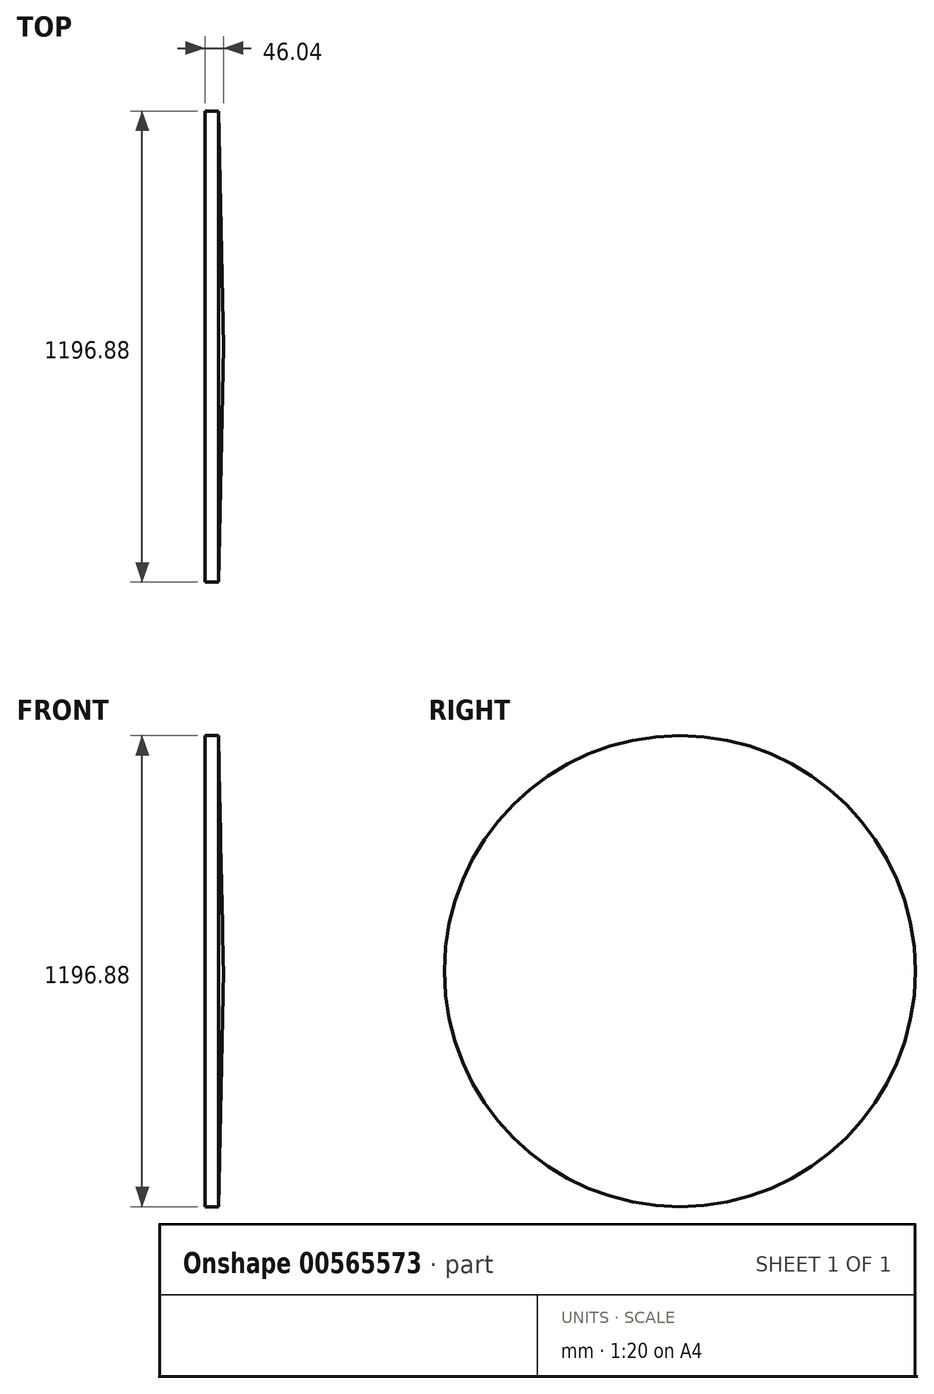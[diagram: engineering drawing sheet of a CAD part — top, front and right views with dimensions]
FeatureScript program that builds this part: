
annotation { "Feature Type Name" : "Feature", "Feature Type Description" : "" }
export const myFeature = defineFeature(function(context is Context, id is Id, definition is map)
    precondition{}
    {
        {
            var Q0;
            Q0=qCreatedBy(makeId("Front.planeOp"),FACE);
            var sketch = newSketch(context, id + "F0", { "sketchPlane" : qUnion([Q0])});
            skPoint(sketch, "E0.middle", {"position": v(0, 0) * mm});
            skLineSegment(sketch, "E1.bottom", {"start": v(-222.31, -598.44) * mm, "end": v(-216.08, -598.44) * mm});
            skLineSegment(sketch, "E1.top", {"start": v(-234.95, 598.44) * mm, "end": v(-230.46, 598.44) * mm});
            skLineSegment(sketch, "E2.bottom", {"start": v(234.95, -632.46) * mm, "end": v(190.65, -632.46) * mm});
            skLineSegment(sketch, "E2.top", {"start": v(222.31, 598.44) * mm, "end": v(188.9, 598.44) * mm});
            skLineSegment(sketch, "E3", {"start": v(0, 0) * mm, "end": v(0, 69.03) * mm});
            skLineSegment(sketch, "E4", {"start": v(-234.95, 0) * mm, "end": v(234.95, 0) * mm});
            skLineSegment(sketch, "E5", {"start": v(-234.95, 598.44) * mm, "end": v(-234.95, 0) * mm});
            skLineSegment(sketch, "E6", {"start": v(-230.46, 598.44) * mm, "end": v(-230.46, 0) * mm});
            skLineSegment(sketch, "E7", {"start": v(188.9, 598.44) * mm, "end": v(188.9, 0) * mm});
            skLineSegment(sketch, "E8", {"start": v(222.31, 598.44) * mm, "end": v(234.95, 0) * mm});
            skArc(sketch, "E9", {"start": v(188.9, 598.44) * mm, "mid": v(-20.78, 523.32) * mm, "end": v(-230.46, 598.44) * mm});
            skLineSegment(sketch, "E10", {"start": v(-20.78, 853.52) * mm, "end": v(-20.78, 343.36) * mm});
            skSolve(sketch);
        }
        {
            var Q0;
            Q0=makeQuery(id+"F0.imprint","IMPRINT",FACE,{"disambiguationData":[TD([[makeQuery(id+"F0.imprint","IMPRINT",EDGE,{"derivedFrom":sQuery(id+"F0.wireOp",EDGE,"E2.top")}),1.0]])]});
            var Q1;
            Q1=makeQuery(id+"F0.imprint","IMPRINT",FACE,{"disambiguationData":[TD([[makeQuery(id+"F0.imprint","IMPRINT",EDGE,{"derivedFrom":sQuery(id+"F0.wireOp",EDGE,"NtezhhEd-afQc-ZzzI-E4Sa-in9W7uB9rLGq")}),-1.0]])]});
            var Q2;
            Q2=sQuery(id+"F0.wireOp",EDGE,"E4");
            revolve(context, id + "F1", {"entities" : qUnion([Q0, Q1]), "axis" : qUnion([Q2]), "revolveType" : RevolveType.FULL});
        }
    });
